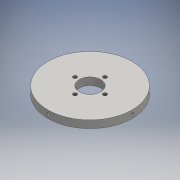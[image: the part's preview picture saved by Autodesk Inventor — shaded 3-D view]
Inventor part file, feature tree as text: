
AUTODESK INVENTOR PART (.ipt)
format: ipt  version: 2016 (Build 200138000, 138)  size: 150,528 bytes
history: native  units: mm
features: thread x8, extrude x6, other x5, sketch x5
ambient origin geometry x8: Origin, YZ Plane, XZ Plane, XY Plane, X Axis, Y Axis, Z Axis, Center Point
bodies: Body1 (feature_tree)
feature tree (24):
  other  "ソリッド1"
  extrude  "押し出し1"  Depth=90.0mm
  extrude  "押し出し2"  Depth=23.0mm
  other  "作業平面1"
  extrude  "押し出し3"  Depth=8.0mm TaperAngle=0.0deg
  other  "作業平面2"
  extrude  "押し出し4"  Depth=16.0mm
  other  "作業平面3"
  extrude  "押し出し5"  Depth=4.0mm
  other  "作業平面4"
  extrude  "押し出し6"  Depth=40.0mm TaperAngle=360.0deg
  thread  "ねじ2"
  thread  "ねじ3"
  thread  "ねじ4"
  thread  "ねじ5"
  thread  "ねじ10"
  thread  "ねじ11"
  thread  "ねじ12"
  thread  "ねじ13"
  sketch  "スケッチ1"
  sketch  "スケッチ3"
  sketch  "スケッチ4"
  sketch  "スケッチ5"
  sketch  "スケッチ6"
